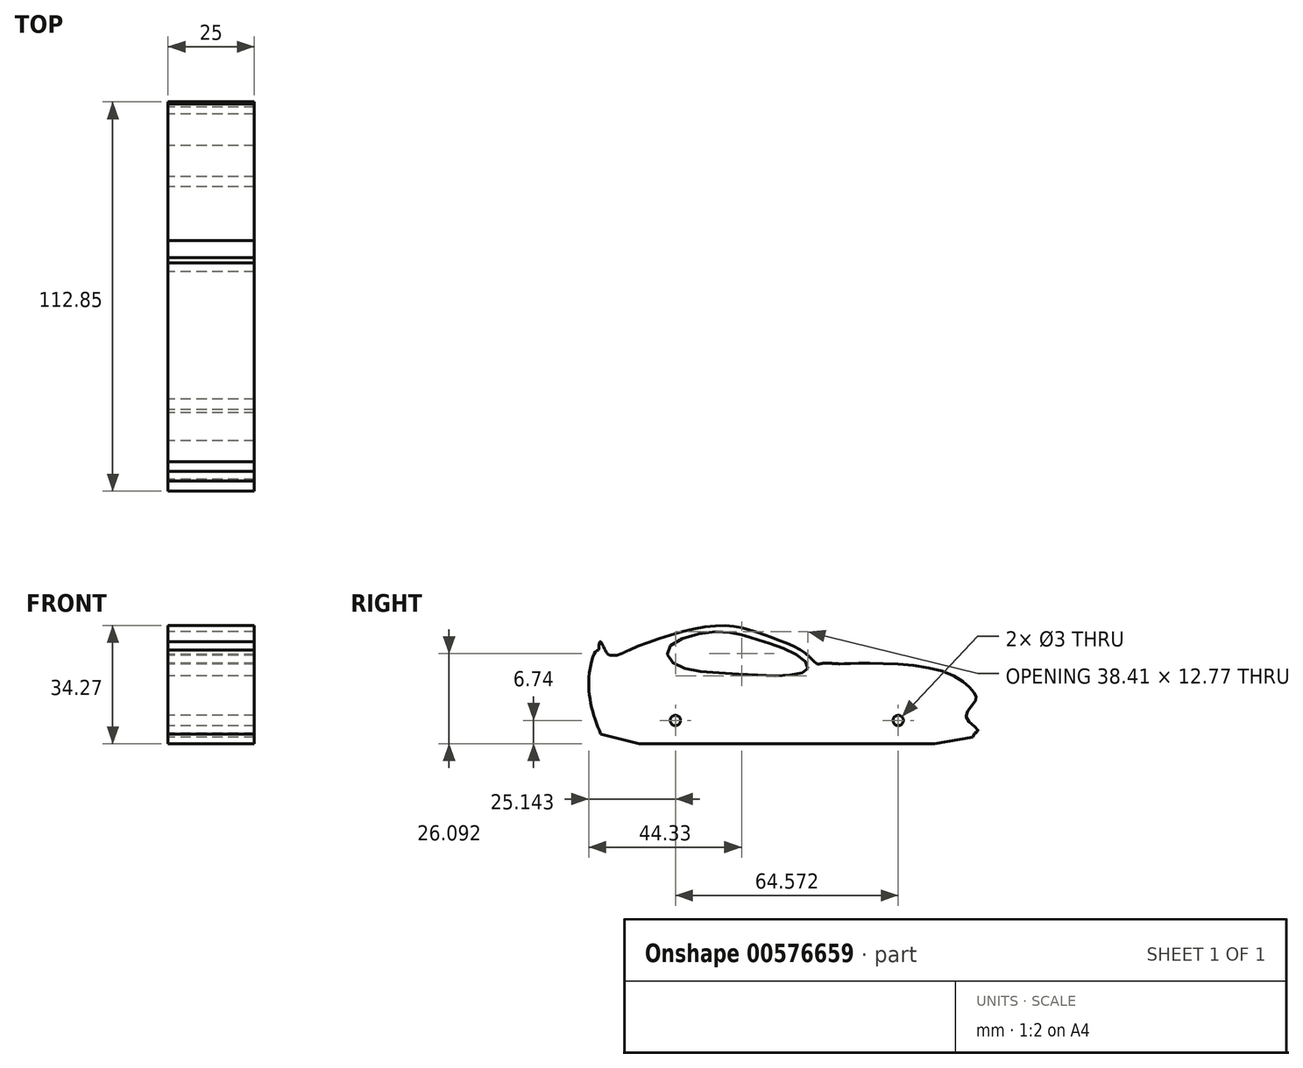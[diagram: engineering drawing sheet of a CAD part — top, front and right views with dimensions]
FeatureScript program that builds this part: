
annotation { "Feature Type Name" : "Feature", "Feature Type Description" : "" }
export const myFeature = defineFeature(function(context is Context, id is Id, definition is map)
    precondition{}
    {
        {
            var Q0;
            Q0=qCreatedBy(makeId("Right.planeOp"),FACE);
            var sketch = newSketch(context, id + "F0", { "sketchPlane" : qUnion([Q0])});
            skCircle(sketch, "E0", {"center": v(-29.06, 0) * mm, "radius": 12.5 * mm, "construction": true});
            skCircle(sketch, "E1", {"center": v(35.51, 0) * mm, "radius": 12.5 * mm, "construction": true});
            skLineSegment(sketch, "E2", {"start": v(-39.59, -6.74) * mm, "end": v(46.04, -6.74) * mm});
            skPoint(sketch, "E3", {"position": v(-39.59, -6.74) * mm});
            skLineSegment(sketch, "E4", {"start": v(-39.59, -6.74) * mm, "end": v(-50.76, -3.95) * mm});
            skPoint(sketch, "E5", {"position": v(46.03, -6.74) * mm});
            skLineSegment(sketch, "E6", {"start": v(46.04, -6.74) * mm, "end": v(57.12, -4.87) * mm});
            skLineSegment(sketch, "E7", {"start": v(57.12, -4.87) * mm, "end": v(57.77, -3.7) * mm});
            skFitSpline(sketch, "E8", {"points": [v(18.44, 16.42) * mm, v(13.38, 16.42) * mm, v(14.08, 15.9) * mm, v(12.67, 16.04) * mm, v(8.32, 19.67) * mm, v(-2.9, 24.69) * mm, v(-16.77, 27.5) * mm, v(-42.4, 20.46) * mm, v(-48.54, 19.13) * mm, v(-50.76, 22.87) * mm, v(-50.76, -3.95) * mm], "startDerivative": vector(-101.38, 7) * mm, "endDerivative": vector(9.2, -229.67) * mm});
            skFitSpline(sketch, "E9", {"points": [v(-42.4, 20.46) * mm, v(-44.96, 19.13) * mm, v(-44.96, 19.13) * mm], "startDerivative": vector(-3.87, -2.03) * mm, "endDerivative": vector(-0.03, 0.01) * mm});
            skFitSpline(sketch, "E10", {"points": [v(-44.96, 19.13) * mm, v(-48.54, 19.13) * mm, v(-51.51, 20.41) * mm, v(-54.2, 10.21) * mm, v(-50.76, -3.95) * mm], "startDerivative": vector(-20.8, -4.14) * mm, "endDerivative": vector(14.3, -37.44) * mm});
            skPoint(sketch, "E11", {"position": v(58.62, -2.67) * mm});
            skPoint(sketch, "E12", {"position": v(55.22, 0.94) * mm});
            skPoint(sketch, "E13", {"position": v(57.77, 5.48) * mm});
            skPoint(sketch, "E14", {"position": v(57.77, 7.65) * mm});
            skPoint(sketch, "E15", {"position": v(49.3, 13.93) * mm});
            skPoint(sketch, "E16", {"position": v(23.72, 16.6) * mm});
            skPoint(sketch, "E17", {"position": v(58.27, -3.4) * mm});
            skFitSpline(sketch, "E18", {"points": [v(57.77, -3.7) * mm, v(58.27, -3.4) * mm, v(58.62, -2.67) * mm, v(55.22, 0.94) * mm, v(57.77, 5.48) * mm, v(57.77, 7.65) * mm, v(49.3, 13.93) * mm, v(23.72, 16.6) * mm, v(18.44, 16.42) * mm], "startDerivative": vector(11.41, 5.84) * mm, "endDerivative": vector(-31.4, -1.7) * mm});
            skFitSpline(sketch, "E19", {"points": [v(9.34, 15.12) * mm, v(4.63, 13.18) * mm, v(-13.63, 13.65) * mm, v(-29.5, 16.5) * mm, v(-30.99, 21.17) * mm, v(-17.67, 25.7) * mm, v(-8.8, 24.6) * mm, v(-4.02, 23.03) * mm, v(6.5, 18.83) * mm, v(9.34, 15.12) * mm]});
            skPoint(sketch, "E20", {"position": v(-8.24, 26.5) * mm});
            skPoint(sketch, "E21", {"position": v(-26.41, 25.9) * mm});
            skPoint(sketch, "E22", {"position": v(-26.72, 23.92) * mm});
            skPoint(sketch, "E23", {"position": v(6.5, 20.83) * mm});
            skPoint(sketch, "E24", {"position": v(12, 16.42) * mm});
            skPoint(sketch, "E25", {"position": v(13.48, 16.55) * mm});
            skFitSpline(sketch, "E26", {"points": [v(13.48, 16.55) * mm, v(12.85, 16.44) * mm, v(12.3, 16.35) * mm, v(12, 16.42) * mm], "startDerivative": vector(-1.66, -0.24) * mm, "endDerivative": vector(-1.07, 0.37) * mm});
            skCircle(sketch, "E27", {"center": v(35.51, 0) * mm, "radius": 1.5 * mm});
            skCircle(sketch, "E28", {"center": v(-29.06, 0) * mm, "radius": 1.5 * mm});
            skSolve(sketch);
        }
        {
            var Q0;
            Q0 = qSketchRegion(id + "F0", true);
            extrude(context, id + "F1", {"entities" : qUnion([Q0]), "depth" : 25 * mm, "offsetDistance" : 25 * mm});
        }
    });
